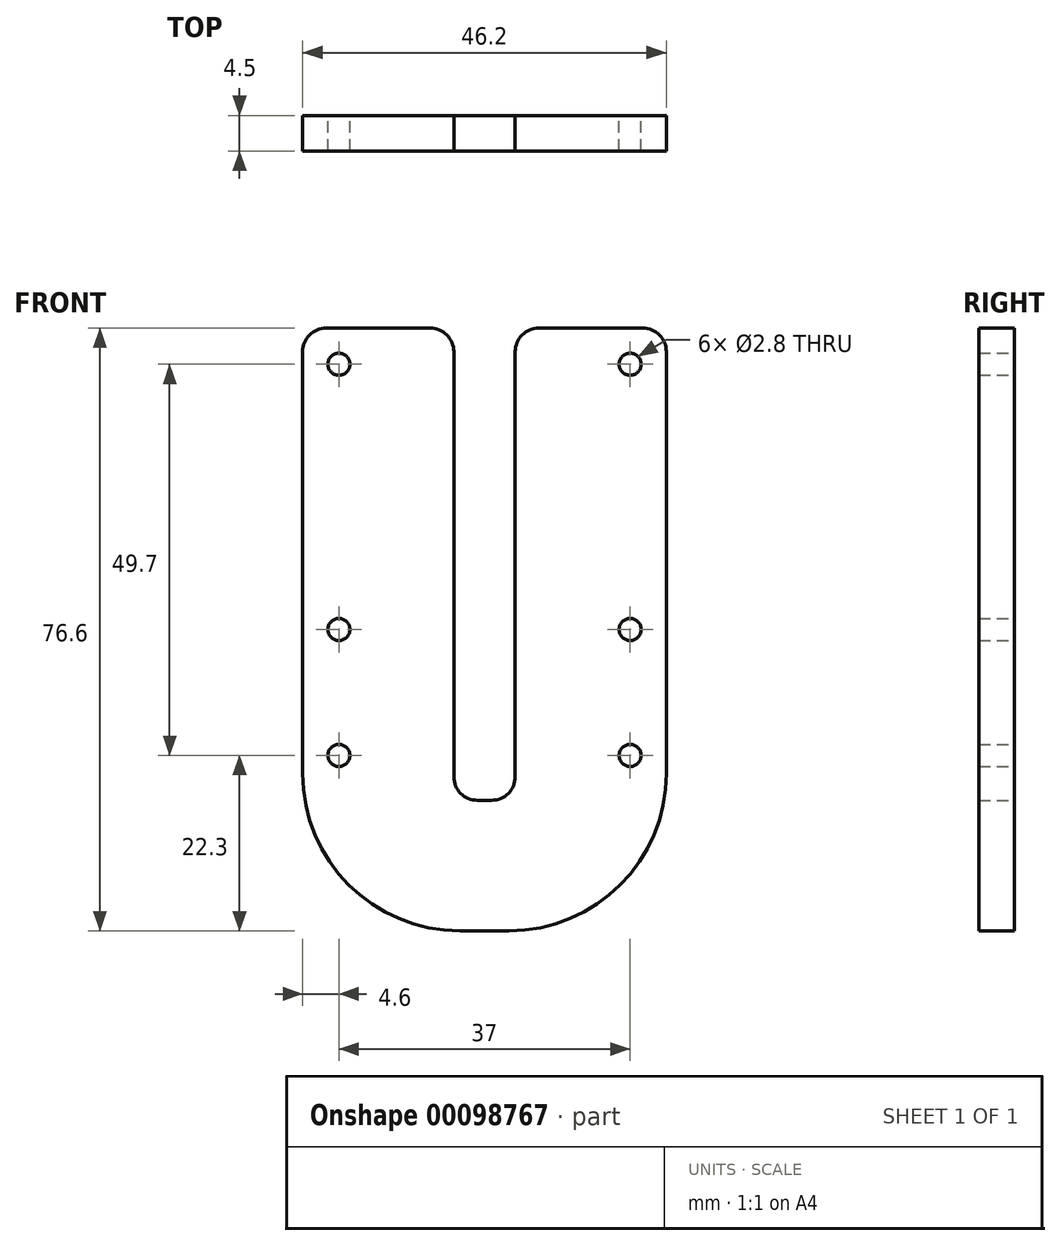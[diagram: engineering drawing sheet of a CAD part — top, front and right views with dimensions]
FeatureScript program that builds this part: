
annotation { "Feature Type Name" : "Feature", "Feature Type Description" : "" }
export const myFeature = defineFeature(function(context is Context, id is Id, definition is map)
    precondition{}
    {
        {
            var Q0;
            Q0=qCreatedBy(makeId("Front.planeOp"),FACE);
            var sketch = newSketch(context, id + "F0", { "sketchPlane" : qUnion([Q0])});
            skLineSegment(sketch, "E0.bottom", {"start": v(23.1, -38.3) * mm, "end": v(-23.1, -38.3) * mm});
            skLineSegment(sketch, "E0.top", {"start": v(23.1, 38.3) * mm, "end": v(3.9, 38.3) * mm});
            skLineSegment(sketch, "E0.left", {"start": v(23.1, -38.3) * mm, "end": v(23.1, 38.3) * mm});
            skLineSegment(sketch, "E0.right", {"start": v(-23.1, -38.3) * mm, "end": v(-23.1, 38.3) * mm});
            skPoint(sketch, "E0.middle", {"position": v(0, 0) * mm});
            skLineSegment(sketch, "E1.top", {"start": v(-3.9, -21.7) * mm, "end": v(3.9, -21.7) * mm});
            skLineSegment(sketch, "E1.left", {"start": v(-3.9, 38.3) * mm, "end": v(-3.9, -21.7) * mm});
            skLineSegment(sketch, "E1.right", {"start": v(3.9, 38.3) * mm, "end": v(3.9, -21.7) * mm});
            skPoint(sketch, "E1.middle", {"position": v(0, 8.3) * mm});
            skLineSegment(sketch, "E2.trimOffspring", {"start": v(-3.9, 38.3) * mm, "end": v(-23.1, 38.3) * mm});
            skLineSegment(sketch, "E3.bottom", {"start": v(18.5, -33.7) * mm, "end": v(-18.5, -33.7) * mm, "construction": true});
            skLineSegment(sketch, "E3.top", {"start": v(18.5, 33.7) * mm, "end": v(-18.5, 33.7) * mm, "construction": true});
            skLineSegment(sketch, "E3.left", {"start": v(18.5, -33.7) * mm, "end": v(18.5, 33.7) * mm, "construction": true});
            skLineSegment(sketch, "E3.right", {"start": v(-18.5, -33.7) * mm, "end": v(-18.5, 33.7) * mm, "construction": true});
            skCircle(sketch, "E4", {"center": v(-18.5, 33.7) * mm, "radius": 1.4 * mm});
            skCircle(sketch, "E5", {"center": v(-18.5, 0) * mm, "radius": 1.4 * mm});
            skCircle(sketch, "E6", {"center": v(-18.5, -16) * mm, "radius": 1.4 * mm});
            skCircle(sketch, "E7", {"center": v(18.5, 0) * mm, "radius": 1.4 * mm});
            skCircle(sketch, "E8", {"center": v(18.5, 33.7) * mm, "radius": 1.4 * mm});
            skCircle(sketch, "E9", {"center": v(18.5, -16) * mm, "radius": 1.4 * mm});
            skSolve(sketch);
        }
        {
            var Q0;
            Q0=makeQuery(id+"F0.imprint","IMPRINT",FACE,{"disambiguationData":[TD([[makeQuery(id+"F0.imprint","IMPRINT",EDGE,{"derivedFrom":sQuery(id+"F0.wireOp",EDGE,"E0.bottom")}),-1.0]])]});
            extrude(context, id + "F1", {"entities" : qUnion([Q0]), "depth" : 4.5 * mm});
        }
        {
            var Q0;
            Q0=makeQuery(id+"F1.opExtrude","SWEPT_EDGE",EDGE,{"disambiguationData":[OSD([sQuery(id+"F0.wireOp",EDGE,"E0.right"),sQuery(id+"F0.wireOp",EDGE,"E2.trimOffspring")])]});
            var Q1;
            Q1=makeQuery(id+"F1.opExtrude","SWEPT_EDGE",EDGE,{"disambiguationData":[OSD([sQuery(id+"F0.wireOp",EDGE,"E0.top"),sQuery(id+"F0.wireOp",EDGE,"E0.left")])]});
            var Q2;
            Q2=makeQuery(id+"F1.opExtrude","SWEPT_EDGE",EDGE,{"disambiguationData":[OSD([sQuery(id+"F0.wireOp",EDGE,"E1.top"),sQuery(id+"F0.wireOp",EDGE,"E1.left")])]});
            var Q3;
            Q3=makeQuery(id+"F1.opExtrude","SWEPT_EDGE",EDGE,{"disambiguationData":[OSD([sQuery(id+"F0.wireOp",EDGE,"E1.top"),sQuery(id+"F0.wireOp",EDGE,"E1.right")])]});
            var Q4;
            Q4=makeQuery(id+"F1.opExtrude","SWEPT_EDGE",EDGE,{"disambiguationData":[OSD([sQuery(id+"F0.wireOp",EDGE,"E1.left"),sQuery(id+"F0.wireOp",EDGE,"E2.trimOffspring")])]});
            var Q5;
            Q5=makeQuery(id+"F1.opExtrude","SWEPT_EDGE",EDGE,{"disambiguationData":[OSD([sQuery(id+"F0.wireOp",EDGE,"E0.top"),sQuery(id+"F0.wireOp",EDGE,"E1.right")])]});
            fillet(context, id + "F2", {"entities" : qUnion([Q0, Q1, Q2, Q3, Q4, Q5]), "radius" : 3 * mm, "tangentPropagation" : true, "allowEdgeOverflow" : false});
        }
        {
            var Q0;
            Q0=makeQuery(id+"F1.opExtrude","SWEPT_EDGE",EDGE,{"disambiguationData":[OSD([sQuery(id+"F0.wireOp",EDGE,"E0.bottom"),sQuery(id+"F0.wireOp",EDGE,"E0.right")])]});
            var Q1;
            Q1=makeQuery(id+"F1.opExtrude","SWEPT_EDGE",EDGE,{"disambiguationData":[OSD([sQuery(id+"F0.wireOp",EDGE,"E0.bottom"),sQuery(id+"F0.wireOp",EDGE,"E0.left")])]});
            fillet(context, id + "F3", {"entities" : qUnion([Q0, Q1]), "radius" : 20 * mm, "tangentPropagation" : true, "allowEdgeOverflow" : false});
        }
    });
